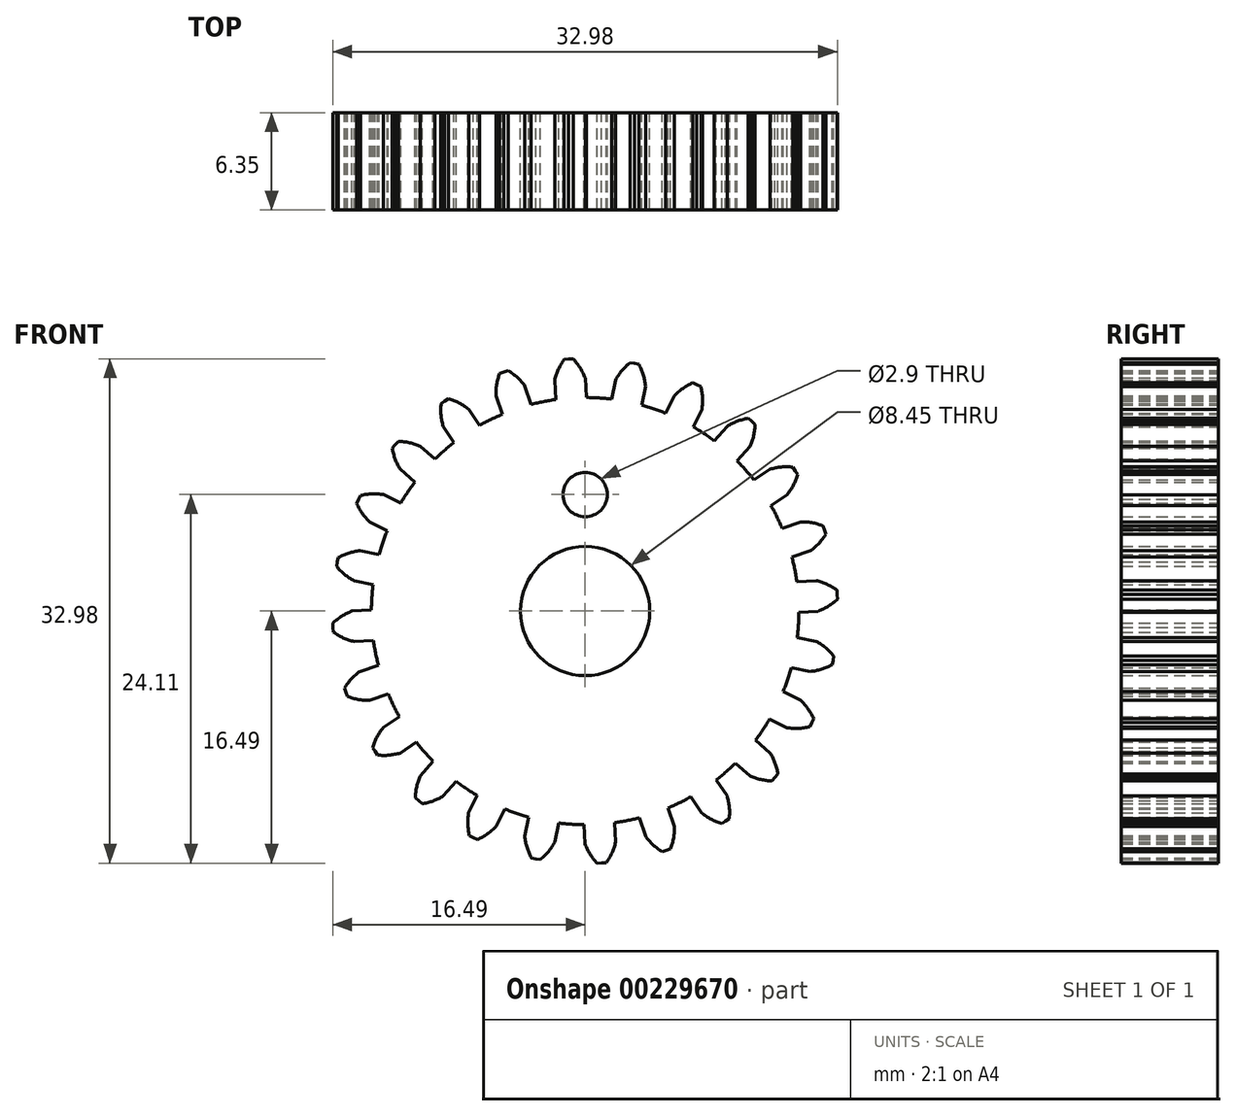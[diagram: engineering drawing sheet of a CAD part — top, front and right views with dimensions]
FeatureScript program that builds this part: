
annotation { "Feature Type Name" : "Feature", "Feature Type Description" : "" }
export const myFeature = defineFeature(function(context is Context, id is Id, definition is map)
    precondition{}
    {
        {
            var Q0;
            Q0=qCreatedBy(makeId("Front.planeOp"),FACE);
            var sketch = newSketch(context, id + "F0", { "sketchPlane" : qUnion([Q0])});
            skCircle(sketch, "E0", {"center": v(0, 0) * mm, "radius": 13.97 * mm});
            skArc(sketch, "E1.trimOffspring", {"start": v(0, 15.24) * mm, "mid": v(-0.33, 15.9) * mm, "end": v(-0.79, 16.5) * mm});
            skLineSegment(sketch, "E2", {"start": v(0, 15.24) * mm, "end": v(0.09, 13.97) * mm});
            skLineSegment(sketch, "E3", {"start": v(-0.79, 16.5) * mm, "end": v(-1.08, 16.48) * mm});
            skLineSegment(sketch, "E4.MirrorCS", {"start": v(-1.37, 16.45) * mm, "end": v(-1.08, 16.48) * mm});
            skArc(sketch, "E5.MirrorCS", {"start": v(-2, 15.1) * mm, "mid": v(-1.75, 15.81) * mm, "end": v(-1.37, 16.45) * mm});
            skLineSegment(sketch, "E6.MirrorCS", {"start": v(-2, 15.1) * mm, "end": v(-1.9, 13.84) * mm});
            skPoint(sketch, "E7.orphan", {"position": v(-1.79, 11.97) * mm});
            skPoint(sketch, "E8.orphan", {"position": v(0.2, 12.1) * mm});
            skLineSegment(sketch, "E9.1.0", {"start": v(-5.84, 14.08) * mm, "end": v(-5.43, 12.87) * mm});
            skArc(sketch, "E9.1.1", {"start": v(-5.84, 14.08) * mm, "mid": v(-5.78, 14.82) * mm, "end": v(-5.59, 15.54) * mm});
            skLineSegment(sketch, "E9.1.2", {"start": v(-5.59, 15.54) * mm, "end": v(-5.3, 15.64) * mm});
            skLineSegment(sketch, "E9.1.3", {"start": v(-5.03, 15.73) * mm, "end": v(-5.3, 15.64) * mm});
            skArc(sketch, "E9.1.4", {"start": v(-3.94, 14.72) * mm, "mid": v(-4.43, 15.28) * mm, "end": v(-5.03, 15.73) * mm});
            skLineSegment(sketch, "E9.1.5", {"start": v(-3.94, 14.72) * mm, "end": v(-3.53, 13.52) * mm});
            skLineSegment(sketch, "E9.2.0", {"start": v(-9.28, 12.09) * mm, "end": v(-8.57, 11.03) * mm});
            skArc(sketch, "E9.2.1", {"start": v(-9.28, 12.09) * mm, "mid": v(-9.42, 12.82) * mm, "end": v(-9.42, 13.56) * mm});
            skLineSegment(sketch, "E9.2.2", {"start": v(-9.42, 13.56) * mm, "end": v(-9.17, 13.73) * mm});
            skLineSegment(sketch, "E9.2.3", {"start": v(-8.93, 13.89) * mm, "end": v(-9.17, 13.73) * mm});
            skArc(sketch, "E9.2.4", {"start": v(-7.62, 13.2) * mm, "mid": v(-8.24, 13.6) * mm, "end": v(-8.93, 13.89) * mm});
            skLineSegment(sketch, "E9.2.5", {"start": v(-7.62, 13.2) * mm, "end": v(-6.9, 12.14) * mm});
            skLineSegment(sketch, "E9.3.0", {"start": v(-12.1, 9.27) * mm, "end": v(-11.14, 8.44) * mm});
            skArc(sketch, "E9.3.1", {"start": v(-12.1, 9.27) * mm, "mid": v(-12.42, 9.94) * mm, "end": v(-12.6, 10.66) * mm});
            skLineSegment(sketch, "E9.3.2", {"start": v(-12.6, 10.66) * mm, "end": v(-12.41, 10.89) * mm});
            skLineSegment(sketch, "E9.3.3", {"start": v(-12.22, 11.1) * mm, "end": v(-12.41, 10.89) * mm});
            skArc(sketch, "E9.3.4", {"start": v(-10.77, 10.78) * mm, "mid": v(-11.48, 11.01) * mm, "end": v(-12.22, 11.1) * mm});
            skLineSegment(sketch, "E9.3.5", {"start": v(-10.77, 10.78) * mm, "end": v(-9.82, 9.94) * mm});
            skLineSegment(sketch, "E9.4.0", {"start": v(-14.08, 5.83) * mm, "end": v(-12.94, 5.27) * mm});
            skArc(sketch, "E9.4.1", {"start": v(-14.08, 5.83) * mm, "mid": v(-14.57, 6.4) * mm, "end": v(-14.94, 7.04) * mm});
            skLineSegment(sketch, "E9.4.2", {"start": v(-14.94, 7.04) * mm, "end": v(-14.8, 7.3) * mm});
            skLineSegment(sketch, "E9.4.3", {"start": v(-14.67, 7.57) * mm, "end": v(-14.8, 7.3) * mm});
            skArc(sketch, "E9.4.4", {"start": v(-13.2, 7.62) * mm, "mid": v(-13.94, 7.67) * mm, "end": v(-14.67, 7.57) * mm});
            skLineSegment(sketch, "E9.4.5", {"start": v(-13.2, 7.62) * mm, "end": v(-12.05, 7.06) * mm});
            skLineSegment(sketch, "E9.5.0", {"start": v(-15.11, 1.99) * mm, "end": v(-13.86, 1.74) * mm});
            skArc(sketch, "E9.5.1", {"start": v(-15.11, 1.99) * mm, "mid": v(-15.73, 2.4) * mm, "end": v(-16.25, 2.93) * mm});
            skLineSegment(sketch, "E9.5.2", {"start": v(-16.25, 2.93) * mm, "end": v(-16.2, 3.22) * mm});
            skLineSegment(sketch, "E9.5.3", {"start": v(-16.13, 3.5) * mm, "end": v(-16.2, 3.22) * mm});
            skArc(sketch, "E9.5.4", {"start": v(-14.72, 3.95) * mm, "mid": v(-15.45, 3.8) * mm, "end": v(-16.13, 3.5) * mm});
            skLineSegment(sketch, "E9.5.5", {"start": v(-14.72, 3.95) * mm, "end": v(-13.47, 3.7) * mm});
            skLineSegment(sketch, "E9.6.0", {"start": v(-15.1, -2) * mm, "end": v(-13.84, -1.9) * mm});
            skArc(sketch, "E9.6.1", {"start": v(-15.1, -2) * mm, "mid": v(-15.81, -1.75) * mm, "end": v(-16.45, -1.37) * mm});
            skLineSegment(sketch, "E9.6.2", {"start": v(-16.45, -1.37) * mm, "end": v(-16.48, -1.08) * mm});
            skLineSegment(sketch, "E9.6.3", {"start": v(-16.5, -0.79) * mm, "end": v(-16.48, -1.08) * mm});
            skArc(sketch, "E9.6.4", {"start": v(-15.24, 0) * mm, "mid": v(-15.9, -0.33) * mm, "end": v(-16.5, -0.79) * mm});
            skLineSegment(sketch, "E9.6.5", {"start": v(-15.24, 0) * mm, "end": v(-13.97, 0.09) * mm});
            skLineSegment(sketch, "E9.7.0", {"start": v(-14.08, -5.84) * mm, "end": v(-12.87, -5.43) * mm});
            skArc(sketch, "E9.7.1", {"start": v(-14.08, -5.84) * mm, "mid": v(-14.82, -5.78) * mm, "end": v(-15.54, -5.59) * mm});
            skLineSegment(sketch, "E9.7.2", {"start": v(-15.54, -5.59) * mm, "end": v(-15.64, -5.3) * mm});
            skLineSegment(sketch, "E9.7.3", {"start": v(-15.73, -5.03) * mm, "end": v(-15.64, -5.3) * mm});
            skArc(sketch, "E9.7.4", {"start": v(-14.72, -3.94) * mm, "mid": v(-15.28, -4.43) * mm, "end": v(-15.73, -5.03) * mm});
            skLineSegment(sketch, "E9.7.5", {"start": v(-14.72, -3.94) * mm, "end": v(-13.52, -3.53) * mm});
            skLineSegment(sketch, "E9.8.0", {"start": v(-12.09, -9.28) * mm, "end": v(-11.03, -8.57) * mm});
            skArc(sketch, "E9.8.1", {"start": v(-12.09, -9.28) * mm, "mid": v(-12.82, -9.42) * mm, "end": v(-13.56, -9.42) * mm});
            skLineSegment(sketch, "E9.8.2", {"start": v(-13.56, -9.42) * mm, "end": v(-13.73, -9.17) * mm});
            skLineSegment(sketch, "E9.8.3", {"start": v(-13.89, -8.93) * mm, "end": v(-13.73, -9.17) * mm});
            skArc(sketch, "E9.8.4", {"start": v(-13.2, -7.62) * mm, "mid": v(-13.6, -8.24) * mm, "end": v(-13.89, -8.93) * mm});
            skLineSegment(sketch, "E9.8.5", {"start": v(-13.2, -7.62) * mm, "end": v(-12.14, -6.9) * mm});
            skLineSegment(sketch, "E9.9.0", {"start": v(-9.27, -12.1) * mm, "end": v(-8.44, -11.14) * mm});
            skArc(sketch, "E9.9.1", {"start": v(-9.27, -12.1) * mm, "mid": v(-9.94, -12.42) * mm, "end": v(-10.66, -12.6) * mm});
            skLineSegment(sketch, "E9.9.2", {"start": v(-10.66, -12.6) * mm, "end": v(-10.89, -12.41) * mm});
            skLineSegment(sketch, "E9.9.3", {"start": v(-11.1, -12.22) * mm, "end": v(-10.89, -12.41) * mm});
            skArc(sketch, "E9.9.4", {"start": v(-10.78, -10.77) * mm, "mid": v(-11.01, -11.48) * mm, "end": v(-11.1, -12.22) * mm});
            skLineSegment(sketch, "E9.9.5", {"start": v(-10.78, -10.77) * mm, "end": v(-9.94, -9.82) * mm});
            skLineSegment(sketch, "E9.10.0", {"start": v(-5.83, -14.08) * mm, "end": v(-5.27, -12.94) * mm});
            skArc(sketch, "E9.10.1", {"start": v(-5.83, -14.08) * mm, "mid": v(-6.4, -14.57) * mm, "end": v(-7.04, -14.94) * mm});
            skLineSegment(sketch, "E9.10.2", {"start": v(-7.04, -14.94) * mm, "end": v(-7.3, -14.8) * mm});
            skLineSegment(sketch, "E9.10.3", {"start": v(-7.57, -14.67) * mm, "end": v(-7.3, -14.8) * mm});
            skArc(sketch, "E9.10.4", {"start": v(-7.62, -13.2) * mm, "mid": v(-7.67, -13.94) * mm, "end": v(-7.57, -14.67) * mm});
            skLineSegment(sketch, "E9.10.5", {"start": v(-7.62, -13.2) * mm, "end": v(-7.06, -12.05) * mm});
            skLineSegment(sketch, "E9.11.0", {"start": v(-1.99, -15.11) * mm, "end": v(-1.74, -13.86) * mm});
            skArc(sketch, "E9.11.1", {"start": v(-1.99, -15.11) * mm, "mid": v(-2.4, -15.73) * mm, "end": v(-2.93, -16.25) * mm});
            skLineSegment(sketch, "E9.11.2", {"start": v(-2.93, -16.25) * mm, "end": v(-3.22, -16.2) * mm});
            skLineSegment(sketch, "E9.11.3", {"start": v(-3.5, -16.13) * mm, "end": v(-3.22, -16.2) * mm});
            skArc(sketch, "E9.11.4", {"start": v(-3.95, -14.72) * mm, "mid": v(-3.8, -15.45) * mm, "end": v(-3.5, -16.13) * mm});
            skLineSegment(sketch, "E9.11.5", {"start": v(-3.95, -14.72) * mm, "end": v(-3.7, -13.47) * mm});
            skLineSegment(sketch, "E9.12.0", {"start": v(2, -15.1) * mm, "end": v(1.9, -13.84) * mm});
            skArc(sketch, "E9.12.1", {"start": v(2, -15.1) * mm, "mid": v(1.75, -15.81) * mm, "end": v(1.37, -16.45) * mm});
            skLineSegment(sketch, "E9.12.2", {"start": v(1.37, -16.45) * mm, "end": v(1.08, -16.48) * mm});
            skLineSegment(sketch, "E9.12.3", {"start": v(0.79, -16.5) * mm, "end": v(1.08, -16.48) * mm});
            skArc(sketch, "E9.12.4", {"start": v(0, -15.24) * mm, "mid": v(0.33, -15.9) * mm, "end": v(0.79, -16.5) * mm});
            skLineSegment(sketch, "E9.12.5", {"start": v(0, -15.24) * mm, "end": v(-0.09, -13.97) * mm});
            skLineSegment(sketch, "E9.13.0", {"start": v(5.84, -14.08) * mm, "end": v(5.43, -12.87) * mm});
            skArc(sketch, "E9.13.1", {"start": v(5.84, -14.08) * mm, "mid": v(5.78, -14.82) * mm, "end": v(5.59, -15.54) * mm});
            skLineSegment(sketch, "E9.13.2", {"start": v(5.59, -15.54) * mm, "end": v(5.3, -15.64) * mm});
            skLineSegment(sketch, "E9.13.3", {"start": v(5.03, -15.73) * mm, "end": v(5.3, -15.64) * mm});
            skArc(sketch, "E9.13.4", {"start": v(3.94, -14.72) * mm, "mid": v(4.43, -15.28) * mm, "end": v(5.03, -15.73) * mm});
            skLineSegment(sketch, "E9.13.5", {"start": v(3.94, -14.72) * mm, "end": v(3.53, -13.52) * mm});
            skLineSegment(sketch, "E9.14.0", {"start": v(9.28, -12.09) * mm, "end": v(8.57, -11.03) * mm});
            skArc(sketch, "E9.14.1", {"start": v(9.28, -12.09) * mm, "mid": v(9.42, -12.82) * mm, "end": v(9.42, -13.56) * mm});
            skLineSegment(sketch, "E9.14.2", {"start": v(9.42, -13.56) * mm, "end": v(9.17, -13.73) * mm});
            skLineSegment(sketch, "E9.14.3", {"start": v(8.93, -13.89) * mm, "end": v(9.17, -13.73) * mm});
            skArc(sketch, "E9.14.4", {"start": v(7.62, -13.2) * mm, "mid": v(8.24, -13.6) * mm, "end": v(8.93, -13.89) * mm});
            skLineSegment(sketch, "E9.14.5", {"start": v(7.62, -13.2) * mm, "end": v(6.9, -12.14) * mm});
            skLineSegment(sketch, "E9.15.0", {"start": v(12.1, -9.27) * mm, "end": v(11.14, -8.44) * mm});
            skArc(sketch, "E9.15.1", {"start": v(12.1, -9.27) * mm, "mid": v(12.42, -9.94) * mm, "end": v(12.6, -10.66) * mm});
            skLineSegment(sketch, "E9.15.2", {"start": v(12.6, -10.66) * mm, "end": v(12.41, -10.89) * mm});
            skLineSegment(sketch, "E9.15.3", {"start": v(12.22, -11.1) * mm, "end": v(12.41, -10.89) * mm});
            skArc(sketch, "E9.15.4", {"start": v(10.77, -10.78) * mm, "mid": v(11.48, -11.01) * mm, "end": v(12.22, -11.1) * mm});
            skLineSegment(sketch, "E9.15.5", {"start": v(10.77, -10.78) * mm, "end": v(9.82, -9.94) * mm});
            skLineSegment(sketch, "E9.16.0", {"start": v(14.08, -5.83) * mm, "end": v(12.94, -5.27) * mm});
            skArc(sketch, "E9.16.1", {"start": v(14.08, -5.83) * mm, "mid": v(14.57, -6.4) * mm, "end": v(14.94, -7.04) * mm});
            skLineSegment(sketch, "E9.16.2", {"start": v(14.94, -7.04) * mm, "end": v(14.8, -7.3) * mm});
            skLineSegment(sketch, "E9.16.3", {"start": v(14.67, -7.57) * mm, "end": v(14.8, -7.3) * mm});
            skArc(sketch, "E9.16.4", {"start": v(13.2, -7.62) * mm, "mid": v(13.94, -7.67) * mm, "end": v(14.67, -7.57) * mm});
            skLineSegment(sketch, "E9.16.5", {"start": v(13.2, -7.62) * mm, "end": v(12.05, -7.06) * mm});
            skLineSegment(sketch, "E9.17.0", {"start": v(15.11, -1.99) * mm, "end": v(13.86, -1.74) * mm});
            skArc(sketch, "E9.17.1", {"start": v(15.11, -1.99) * mm, "mid": v(15.73, -2.4) * mm, "end": v(16.25, -2.93) * mm});
            skLineSegment(sketch, "E9.17.2", {"start": v(16.25, -2.93) * mm, "end": v(16.2, -3.22) * mm});
            skLineSegment(sketch, "E9.17.3", {"start": v(16.13, -3.5) * mm, "end": v(16.2, -3.22) * mm});
            skArc(sketch, "E9.17.4", {"start": v(14.72, -3.95) * mm, "mid": v(15.45, -3.8) * mm, "end": v(16.13, -3.5) * mm});
            skLineSegment(sketch, "E9.17.5", {"start": v(14.72, -3.95) * mm, "end": v(13.47, -3.7) * mm});
            skLineSegment(sketch, "E9.18.0", {"start": v(15.1, 2) * mm, "end": v(13.84, 1.9) * mm});
            skArc(sketch, "E9.18.1", {"start": v(15.1, 2) * mm, "mid": v(15.81, 1.75) * mm, "end": v(16.45, 1.37) * mm});
            skLineSegment(sketch, "E9.18.2", {"start": v(16.45, 1.37) * mm, "end": v(16.48, 1.08) * mm});
            skLineSegment(sketch, "E9.18.3", {"start": v(16.5, 0.79) * mm, "end": v(16.48, 1.08) * mm});
            skArc(sketch, "E9.18.4", {"start": v(15.24, 0) * mm, "mid": v(15.9, 0.33) * mm, "end": v(16.5, 0.79) * mm});
            skLineSegment(sketch, "E9.18.5", {"start": v(15.24, 0) * mm, "end": v(13.97, -0.09) * mm});
            skLineSegment(sketch, "E9.19.0", {"start": v(14.08, 5.84) * mm, "end": v(12.87, 5.43) * mm});
            skArc(sketch, "E9.19.1", {"start": v(14.08, 5.84) * mm, "mid": v(14.82, 5.78) * mm, "end": v(15.54, 5.59) * mm});
            skLineSegment(sketch, "E9.19.2", {"start": v(15.54, 5.59) * mm, "end": v(15.64, 5.3) * mm});
            skLineSegment(sketch, "E9.19.3", {"start": v(15.73, 5.03) * mm, "end": v(15.64, 5.3) * mm});
            skArc(sketch, "E9.19.4", {"start": v(14.72, 3.94) * mm, "mid": v(15.28, 4.43) * mm, "end": v(15.73, 5.03) * mm});
            skLineSegment(sketch, "E9.19.5", {"start": v(14.72, 3.94) * mm, "end": v(13.52, 3.53) * mm});
            skLineSegment(sketch, "E9.20.0", {"start": v(12.09, 9.28) * mm, "end": v(11.03, 8.57) * mm});
            skArc(sketch, "E9.20.1", {"start": v(12.09, 9.28) * mm, "mid": v(12.82, 9.42) * mm, "end": v(13.56, 9.42) * mm});
            skLineSegment(sketch, "E9.20.2", {"start": v(13.56, 9.42) * mm, "end": v(13.73, 9.17) * mm});
            skLineSegment(sketch, "E9.20.3", {"start": v(13.89, 8.93) * mm, "end": v(13.73, 9.17) * mm});
            skArc(sketch, "E9.20.4", {"start": v(13.2, 7.62) * mm, "mid": v(13.6, 8.24) * mm, "end": v(13.89, 8.93) * mm});
            skLineSegment(sketch, "E9.20.5", {"start": v(13.2, 7.62) * mm, "end": v(12.14, 6.9) * mm});
            skLineSegment(sketch, "E9.21.0", {"start": v(9.27, 12.1) * mm, "end": v(8.44, 11.14) * mm});
            skArc(sketch, "E9.21.1", {"start": v(9.27, 12.1) * mm, "mid": v(9.94, 12.42) * mm, "end": v(10.66, 12.6) * mm});
            skLineSegment(sketch, "E9.21.2", {"start": v(10.66, 12.6) * mm, "end": v(10.89, 12.41) * mm});
            skLineSegment(sketch, "E9.21.3", {"start": v(11.1, 12.22) * mm, "end": v(10.89, 12.41) * mm});
            skArc(sketch, "E9.21.4", {"start": v(10.78, 10.77) * mm, "mid": v(11.01, 11.48) * mm, "end": v(11.1, 12.22) * mm});
            skLineSegment(sketch, "E9.21.5", {"start": v(10.78, 10.77) * mm, "end": v(9.94, 9.82) * mm});
            skLineSegment(sketch, "E9.22.0", {"start": v(5.83, 14.08) * mm, "end": v(5.27, 12.94) * mm});
            skArc(sketch, "E9.22.1", {"start": v(5.83, 14.08) * mm, "mid": v(6.4, 14.57) * mm, "end": v(7.04, 14.94) * mm});
            skLineSegment(sketch, "E9.22.2", {"start": v(7.04, 14.94) * mm, "end": v(7.3, 14.8) * mm});
            skLineSegment(sketch, "E9.22.3", {"start": v(7.57, 14.67) * mm, "end": v(7.3, 14.8) * mm});
            skArc(sketch, "E9.22.4", {"start": v(7.62, 13.2) * mm, "mid": v(7.67, 13.94) * mm, "end": v(7.57, 14.67) * mm});
            skLineSegment(sketch, "E9.22.5", {"start": v(7.62, 13.2) * mm, "end": v(7.06, 12.05) * mm});
            skLineSegment(sketch, "E9.23.0", {"start": v(1.99, 15.11) * mm, "end": v(1.74, 13.86) * mm});
            skArc(sketch, "E9.23.1", {"start": v(1.99, 15.11) * mm, "mid": v(2.4, 15.73) * mm, "end": v(2.93, 16.25) * mm});
            skLineSegment(sketch, "E9.23.2", {"start": v(2.93, 16.25) * mm, "end": v(3.22, 16.2) * mm});
            skLineSegment(sketch, "E9.23.3", {"start": v(3.5, 16.13) * mm, "end": v(3.22, 16.2) * mm});
            skArc(sketch, "E9.23.4", {"start": v(3.95, 14.72) * mm, "mid": v(3.8, 15.45) * mm, "end": v(3.5, 16.13) * mm});
            skLineSegment(sketch, "E9.23.5", {"start": v(3.95, 14.72) * mm, "end": v(3.7, 13.47) * mm});
            skCircle(sketch, "E10", {"center": v(0, 0) * mm, "radius": 4.22 * mm});
            skLineSegment(sketch, "E11", {"start": v(0, 0) * mm, "end": v(0, 7.62) * mm, "construction": true});
            skCircle(sketch, "E12", {"center": v(0, 7.62) * mm, "radius": 1.45 * mm});
            skSolve(sketch);
        }
        {
            var Q0;
            Q0 = qSketchRegion(id + "F0", true);
            var Q1;
            Q1=makeQuery(id+"F0.imprint","IMPRINT",FACE,{"disambiguationData":[TD([[makeQuery(id+"F0.imprint","IMPRINT",EDGE,{"derivedFrom":sQuery(id+"F0.wireOp",EDGE,"E10")}),-1.0]])]});
            extrude(context, id + "F1", {"entities" : qUnion([Q0, Q1]), "depth" : 6.35 * mm});
        }
    });
